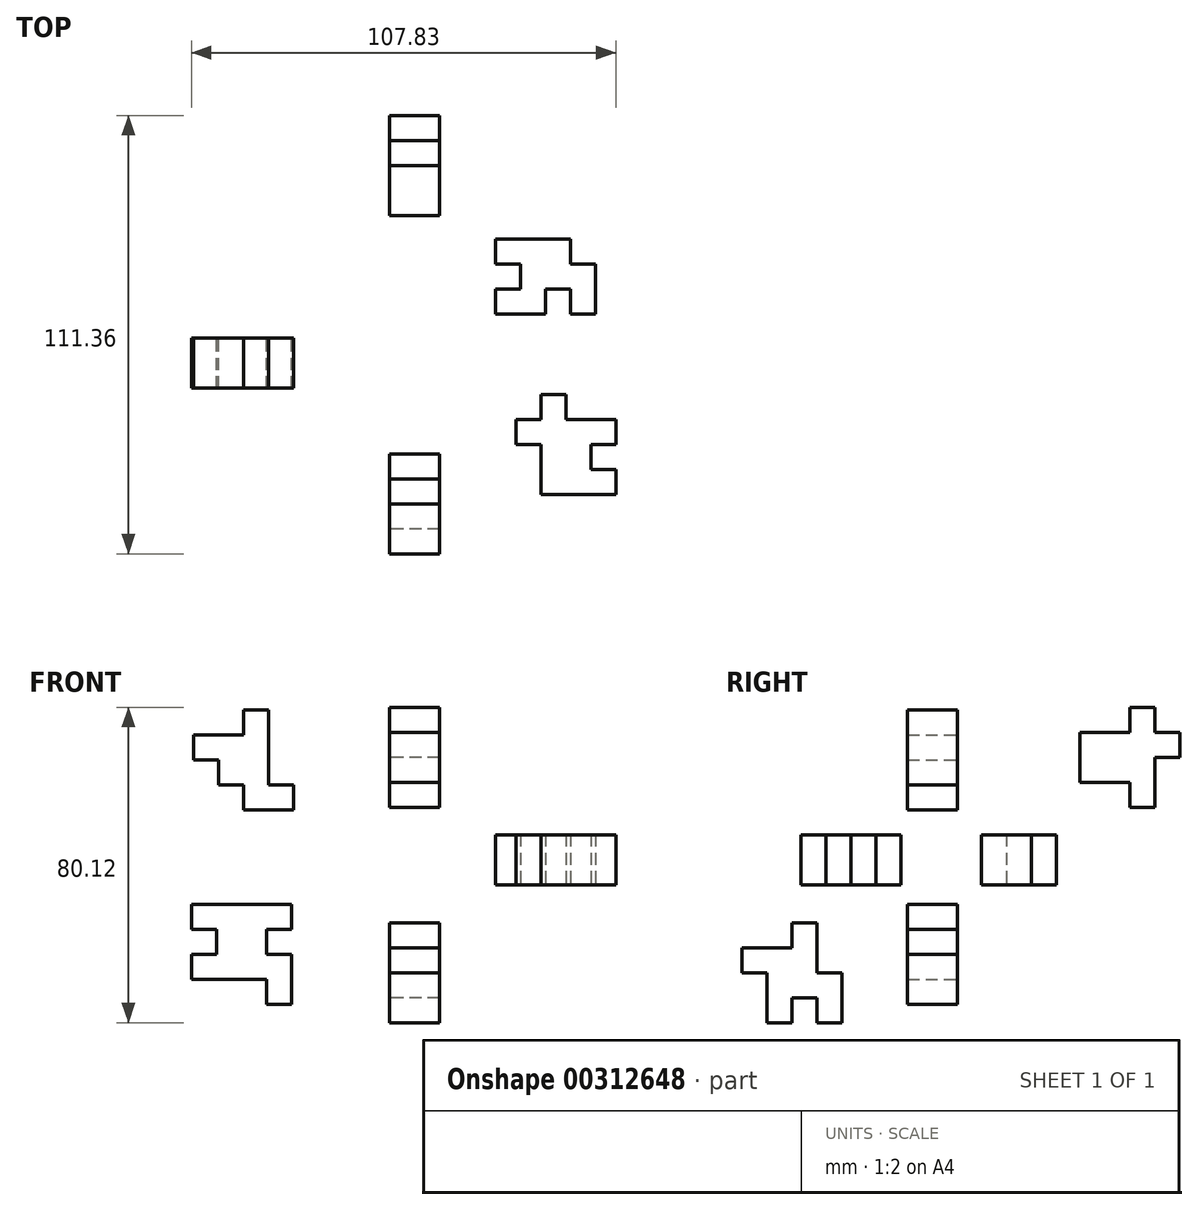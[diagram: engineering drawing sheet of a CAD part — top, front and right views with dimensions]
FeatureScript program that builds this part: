
annotation { "Feature Type Name" : "Feature", "Feature Type Description" : "" }
export const myFeature = defineFeature(function(context is Context, id is Id, definition is map)
    precondition{}
    {
        {
            var Q0;
            Q0=qCreatedBy(makeId("Front.planeOp"),FACE);
            var sketch = newSketch(context, id + "F0", { "sketchPlane" : qUnion([Q0])});
            skLineSegment(sketch, "E0", {"start": v(-43.4, 38.14) * mm, "end": v(-37.06, 38.14) * mm});
            skLineSegment(sketch, "E1", {"start": v(-37.06, 38.14) * mm, "end": v(-37.06, 19.1) * mm});
            skLineSegment(sketch, "E2", {"start": v(-37.06, 19.1) * mm, "end": v(-30.7, 19.1) * mm});
            skLineSegment(sketch, "E3", {"start": v(-30.7, 19.1) * mm, "end": v(-30.7, 12.74) * mm});
            skLineSegment(sketch, "E4", {"start": v(-30.7, 12.74) * mm, "end": v(-43.4, 12.74) * mm});
            skLineSegment(sketch, "E5", {"start": v(-43.4, 12.74) * mm, "end": v(-43.4, 19.1) * mm});
            skLineSegment(sketch, "E6", {"start": v(-43.4, 19.1) * mm, "end": v(-49.76, 19.1) * mm});
            skLineSegment(sketch, "E7", {"start": v(-49.76, 19.1) * mm, "end": v(-49.76, 25.44) * mm});
            skLineSegment(sketch, "E8", {"start": v(-49.76, 25.44) * mm, "end": v(-56.1, 25.44) * mm});
            skLineSegment(sketch, "E9", {"start": v(-56.1, 25.44) * mm, "end": v(-56.1, 31.8) * mm});
            skLineSegment(sketch, "E10", {"start": v(-56.1, 31.8) * mm, "end": v(-43.4, 31.8) * mm});
            skLineSegment(sketch, "E11", {"start": v(-43.4, 38.14) * mm, "end": v(-43.4, 31.8) * mm});
            skSolve(sketch);
        }
        {
            var Q0;
            Q0=makeQuery(id+"F0.imprint","IMPRINT",FACE,{"disambiguationData":[TD([[makeQuery(id+"F0.imprint","IMPRINT",EDGE,{"derivedFrom":sQuery(id+"F0.wireOp",EDGE,"E0")}),-1.0]])]});
            extrude(context, id + "F1", {"entities" : qUnion([Q0]), "endBound" : BoundingType.SYMMETRIC, "depth" : 12.7 * mm});
        }
        {
            var Q0;
            Q0=qCreatedBy(makeId("Top.planeOp"),FACE);
            var sketch = newSketch(context, id + "F2", { "sketchPlane" : qUnion([Q0])});
            skLineSegment(sketch, "E12", {"start": v(20.55, 31.5) * mm, "end": v(39.6, 31.5) * mm});
            skLineSegment(sketch, "E13", {"start": v(20.55, 31.5) * mm, "end": v(20.55, 25.14) * mm});
            skLineSegment(sketch, "E14", {"start": v(20.55, 25.14) * mm, "end": v(26.9, 25.14) * mm});
            skLineSegment(sketch, "E15", {"start": v(26.9, 25.14) * mm, "end": v(26.9, 18.8) * mm});
            skLineSegment(sketch, "E16", {"start": v(26.9, 18.8) * mm, "end": v(20.55, 18.8) * mm});
            skLineSegment(sketch, "E17", {"start": v(20.55, 18.8) * mm, "end": v(20.55, 12.44) * mm});
            skLineSegment(sketch, "E18", {"start": v(20.55, 12.44) * mm, "end": v(33.25, 12.44) * mm});
            skLineSegment(sketch, "E19", {"start": v(33.25, 12.44) * mm, "end": v(33.25, 18.8) * mm});
            skLineSegment(sketch, "E20", {"start": v(33.25, 18.8) * mm, "end": v(39.6, 18.8) * mm});
            skLineSegment(sketch, "E21", {"start": v(39.6, 18.8) * mm, "end": v(39.6, 12.44) * mm});
            skLineSegment(sketch, "E22", {"start": v(39.6, 12.44) * mm, "end": v(45.95, 12.44) * mm});
            skLineSegment(sketch, "E23", {"start": v(45.95, 12.44) * mm, "end": v(45.95, 25.14) * mm});
            skLineSegment(sketch, "E24", {"start": v(45.95, 25.14) * mm, "end": v(39.6, 25.14) * mm});
            skLineSegment(sketch, "E25", {"start": v(39.6, 25.14) * mm, "end": v(39.6, 31.5) * mm});
            skSolve(sketch);
        }
        {
            var Q0;
            Q0=makeQuery(id+"F2.imprint","IMPRINT",FACE,{"disambiguationData":[TD([[makeQuery(id+"F2.imprint","IMPRINT",EDGE,{"derivedFrom":sQuery(id+"F2.wireOp",EDGE,"E12")}),-1.0]])]});
            extrude(context, id + "F3", {"entities" : qUnion([Q0]), "endBound" : BoundingType.SYMMETRIC, "depth" : 12.7 * mm});
        }
        {
            var Q0;
            Q0=qCreatedBy(makeId("Right.planeOp"),FACE);
            var sketch = newSketch(context, id + "F4", { "sketchPlane" : qUnion([Q0])});
            skLineSegment(sketch, "E26", {"start": v(50.16, 38.75) * mm, "end": v(56.5, 38.75) * mm});
            skLineSegment(sketch, "E27", {"start": v(56.5, 38.75) * mm, "end": v(56.5, 32.4) * mm});
            skLineSegment(sketch, "E28", {"start": v(56.5, 32.4) * mm, "end": v(62.86, 32.4) * mm});
            skLineSegment(sketch, "E29", {"start": v(62.86, 32.4) * mm, "end": v(62.86, 26.05) * mm});
            skLineSegment(sketch, "E30", {"start": v(62.86, 26.05) * mm, "end": v(56.5, 26.05) * mm});
            skLineSegment(sketch, "E31", {"start": v(56.5, 26.05) * mm, "end": v(56.5, 13.35) * mm});
            skLineSegment(sketch, "E32", {"start": v(56.5, 13.35) * mm, "end": v(50.16, 13.35) * mm});
            skLineSegment(sketch, "E33", {"start": v(50.16, 13.35) * mm, "end": v(50.16, 19.7) * mm});
            skLineSegment(sketch, "E34", {"start": v(50.16, 19.7) * mm, "end": v(37.46, 19.7) * mm});
            skLineSegment(sketch, "E35", {"start": v(37.46, 19.7) * mm, "end": v(37.46, 32.4) * mm});
            skLineSegment(sketch, "E36", {"start": v(37.46, 32.4) * mm, "end": v(50.16, 32.4) * mm});
            skLineSegment(sketch, "E37", {"start": v(50.16, 32.4) * mm, "end": v(50.16, 38.75) * mm});
            skSolve(sketch);
        }
        {
            var Q0;
            Q0=makeQuery(id+"F4.imprint","IMPRINT",FACE,{"disambiguationData":[TD([[makeQuery(id+"F4.imprint","IMPRINT",EDGE,{"derivedFrom":sQuery(id+"F4.wireOp",EDGE,"E26")}),-1.0]])]});
            extrude(context, id + "F5", {"entities" : qUnion([Q0]), "endBound" : BoundingType.SYMMETRIC, "depth" : 12.7 * mm});
        }
        {
            var Q0;
            Q0=qCreatedBy(makeId("Front.planeOp"),FACE);
            var sketch = newSketch(context, id + "F6", { "sketchPlane" : qUnion([Q0])});
            skLineSegment(sketch, "E38", {"start": v(-31.3, -11.36) * mm, "end": v(-56.7, -11.36) * mm});
            skLineSegment(sketch, "E39", {"start": v(-56.7, -11.36) * mm, "end": v(-56.7, -17.7) * mm});
            skLineSegment(sketch, "E40", {"start": v(-56.7, -17.7) * mm, "end": v(-50.35, -17.7) * mm});
            skLineSegment(sketch, "E41", {"start": v(-50.35, -17.7) * mm, "end": v(-50.35, -24.06) * mm});
            skLineSegment(sketch, "E42", {"start": v(-50.35, -24.06) * mm, "end": v(-56.7, -24.06) * mm});
            skLineSegment(sketch, "E43", {"start": v(-56.7, -24.06) * mm, "end": v(-56.7, -30.4) * mm});
            skLineSegment(sketch, "E44", {"start": v(-56.7, -30.4) * mm, "end": v(-37.65, -30.4) * mm});
            skLineSegment(sketch, "E45", {"start": v(-37.65, -30.4) * mm, "end": v(-37.65, -36.76) * mm});
            skLineSegment(sketch, "E46", {"start": v(-37.65, -36.76) * mm, "end": v(-31.3, -36.76) * mm});
            skLineSegment(sketch, "E47", {"start": v(-31.3, -36.76) * mm, "end": v(-31.3, -24.06) * mm});
            skLineSegment(sketch, "E48", {"start": v(-31.3, -24.06) * mm, "end": v(-37.65, -24.06) * mm});
            skLineSegment(sketch, "E49", {"start": v(-37.65, -24.06) * mm, "end": v(-37.65, -17.7) * mm});
            skLineSegment(sketch, "E50", {"start": v(-37.65, -17.7) * mm, "end": v(-31.3, -17.7) * mm});
            skLineSegment(sketch, "E51", {"start": v(-31.3, -17.7) * mm, "end": v(-31.3, -11.36) * mm});
            skSolve(sketch);
        }
        {
            var Q0;
            Q0=makeQuery(id+"F6.imprint","IMPRINT",FACE,{"disambiguationData":[TD([[makeQuery(id+"F6.imprint","IMPRINT",EDGE,{"derivedFrom":sQuery(id+"F6.wireOp",EDGE,"E38")}),1.0]])]});
            extrude(context, id + "F7", {"entities" : qUnion([Q0]), "endBound" : BoundingType.SYMMETRIC, "depth" : 12.7 * mm});
        }
        {
            var Q0;
            Q0=qCreatedBy(makeId("Top.planeOp"),FACE);
            var sketch = newSketch(context, id + "F8", { "sketchPlane" : qUnion([Q0])});
            skLineSegment(sketch, "E52", {"start": v(32.08, -20.79) * mm, "end": v(32.08, -33.49) * mm});
            skLineSegment(sketch, "E53", {"start": v(32.08, -33.49) * mm, "end": v(51.13, -33.49) * mm});
            skLineSegment(sketch, "E54", {"start": v(51.13, -33.49) * mm, "end": v(51.13, -27.14) * mm});
            skLineSegment(sketch, "E55", {"start": v(51.13, -27.14) * mm, "end": v(44.78, -27.14) * mm});
            skLineSegment(sketch, "E56", {"start": v(44.78, -27.14) * mm, "end": v(44.78, -20.79) * mm});
            skLineSegment(sketch, "E57", {"start": v(44.78, -20.79) * mm, "end": v(51.13, -20.79) * mm});
            skLineSegment(sketch, "E58", {"start": v(51.13, -20.79) * mm, "end": v(51.13, -14.44) * mm});
            skLineSegment(sketch, "E59", {"start": v(51.13, -14.44) * mm, "end": v(38.43, -14.44) * mm});
            skLineSegment(sketch, "E60", {"start": v(38.43, -14.44) * mm, "end": v(38.43, -8.09) * mm});
            skLineSegment(sketch, "E61", {"start": v(38.43, -8.09) * mm, "end": v(32.08, -8.09) * mm});
            skLineSegment(sketch, "E62", {"start": v(32.08, -8.09) * mm, "end": v(32.08, -14.44) * mm});
            skLineSegment(sketch, "E63", {"start": v(32.08, -14.44) * mm, "end": v(25.73, -14.44) * mm});
            skLineSegment(sketch, "E64", {"start": v(25.73, -14.44) * mm, "end": v(25.73, -20.79) * mm});
            skLineSegment(sketch, "E65", {"start": v(25.73, -20.79) * mm, "end": v(32.08, -20.79) * mm});
            skSolve(sketch);
        }
        {
            var Q0;
            Q0=makeQuery(id+"F8.imprint","IMPRINT",FACE,{"disambiguationData":[TD([[makeQuery(id+"F8.imprint","IMPRINT",EDGE,{"derivedFrom":sQuery(id+"F8.wireOp",EDGE,"E52")}),1.0]])]});
            extrude(context, id + "F9", {"entities" : qUnion([Q0]), "endBound" : BoundingType.SYMMETRIC, "depth" : 12.7 * mm});
        }
        {
            var Q0;
            Q0=qCreatedBy(makeId("Right.planeOp"),FACE);
            var sketch = newSketch(context, id + "F10", { "sketchPlane" : qUnion([Q0])});
            skLineSegment(sketch, "E66", {"start": v(-29.45, -15.97) * mm, "end": v(-29.45, -28.67) * mm});
            skLineSegment(sketch, "E67", {"start": v(-29.45, -28.67) * mm, "end": v(-23.1, -28.67) * mm});
            skLineSegment(sketch, "E68", {"start": v(-23.1, -28.67) * mm, "end": v(-23.1, -41.37) * mm});
            skLineSegment(sketch, "E69", {"start": v(-23.1, -41.37) * mm, "end": v(-29.45, -41.37) * mm});
            skLineSegment(sketch, "E70", {"start": v(-29.45, -41.37) * mm, "end": v(-29.45, -35.02) * mm});
            skLineSegment(sketch, "E71", {"start": v(-29.45, -35.02) * mm, "end": v(-35.8, -35.02) * mm});
            skLineSegment(sketch, "E72", {"start": v(-35.8, -35.02) * mm, "end": v(-35.8, -41.37) * mm});
            skLineSegment(sketch, "E73", {"start": v(-35.8, -41.37) * mm, "end": v(-42.15, -41.37) * mm});
            skLineSegment(sketch, "E74", {"start": v(-42.15, -41.37) * mm, "end": v(-42.15, -28.67) * mm});
            skLineSegment(sketch, "E75", {"start": v(-42.15, -28.67) * mm, "end": v(-48.5, -28.67) * mm});
            skLineSegment(sketch, "E76", {"start": v(-48.5, -28.67) * mm, "end": v(-48.5, -22.32) * mm});
            skLineSegment(sketch, "E77", {"start": v(-48.5, -22.32) * mm, "end": v(-35.8, -22.32) * mm});
            skLineSegment(sketch, "E78", {"start": v(-35.8, -22.32) * mm, "end": v(-35.8, -15.97) * mm});
            skLineSegment(sketch, "E79", {"start": v(-35.8, -15.97) * mm, "end": v(-29.45, -15.97) * mm});
            skSolve(sketch);
        }
        {
            var Q0;
            Q0=makeQuery(id+"F10.imprint","IMPRINT",FACE,{"disambiguationData":[TD([[makeQuery(id+"F10.imprint","IMPRINT",EDGE,{"derivedFrom":sQuery(id+"F10.wireOp",EDGE,"E66")}),-1.0]])]});
            extrude(context, id + "F11", {"entities" : qUnion([Q0]), "endBound" : BoundingType.SYMMETRIC, "depth" : 12.7 * mm});
        }
    });
